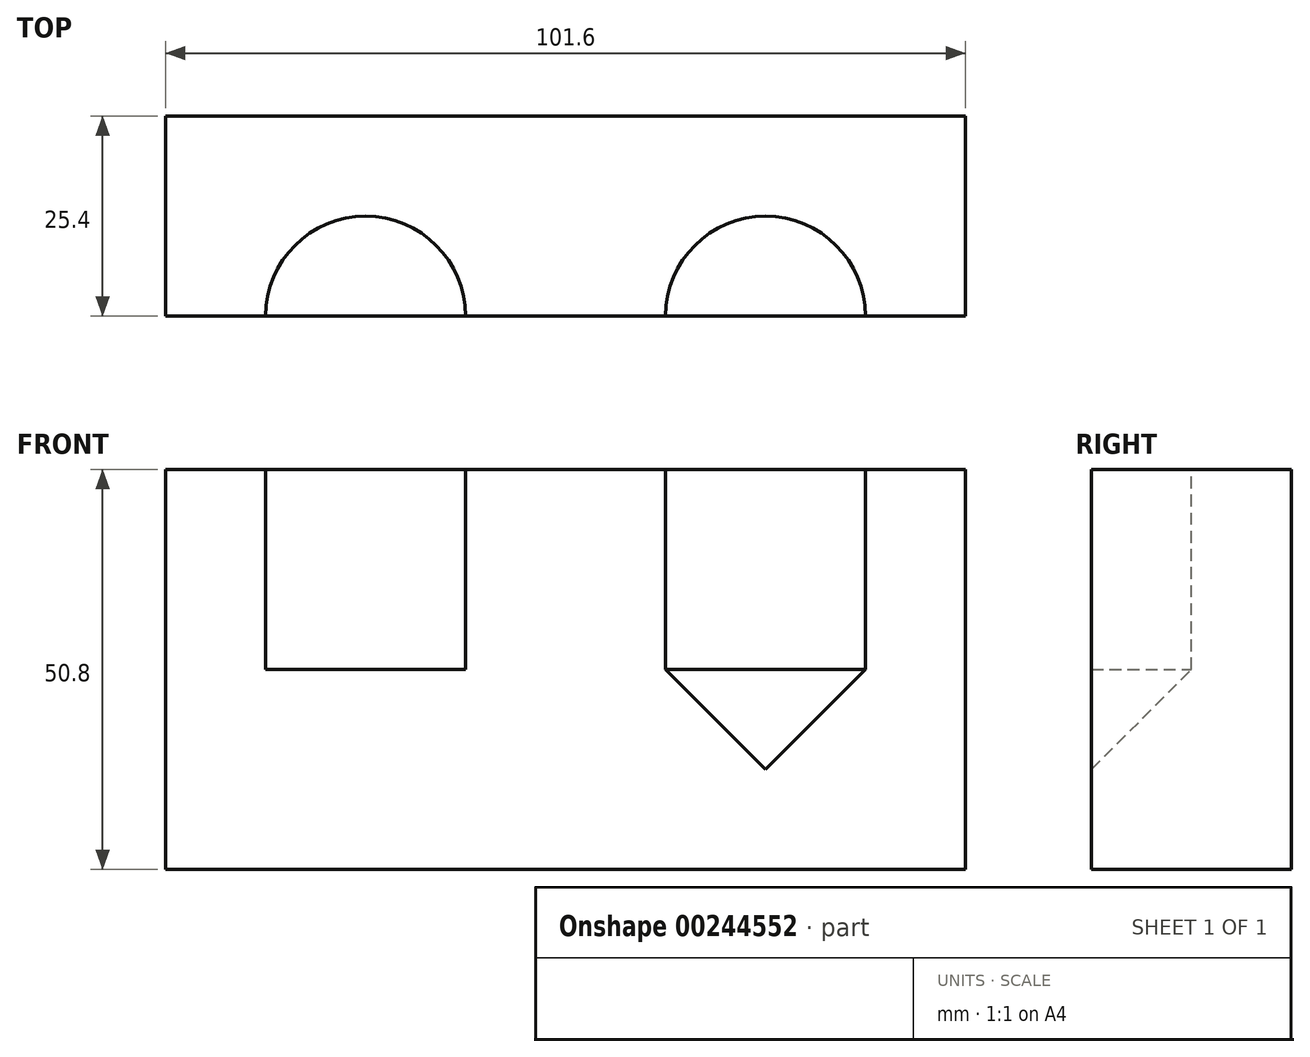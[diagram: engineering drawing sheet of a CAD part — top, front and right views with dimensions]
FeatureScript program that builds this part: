
annotation { "Feature Type Name" : "Feature", "Feature Type Description" : "" }
export const myFeature = defineFeature(function(context is Context, id is Id, definition is map)
    precondition{}
    {
        {
            var Q0;
            Q0=qCreatedBy(makeId("Top.planeOp"),FACE);
            var sketch = newSketch(context, id + "F0", { "sketchPlane" : qUnion([Q0])});
            skLineSegment(sketch, "E0.bottom", {"start": v(50.8, -25.4) * mm, "end": v(-50.8, -25.4) * mm});
            skLineSegment(sketch, "E0.top", {"start": v(50.8, 25.4) * mm, "end": v(-50.8, 25.4) * mm});
            skLineSegment(sketch, "E0.left", {"start": v(50.8, -25.4) * mm, "end": v(50.8, 25.4) * mm});
            skLineSegment(sketch, "E0.right", {"start": v(-50.8, -25.4) * mm, "end": v(-50.8, 25.4) * mm});
            skPoint(sketch, "E0.middle", {"position": v(0, 0) * mm});
            skSolve(sketch);
        }
        {
            var Q0;
            Q0 = qSketchRegion(id + "F0", true);
            extrude(context, id + "F1", {"entities" : qUnion([Q0]), "depth" : 50.8 * mm});
        }
        {
            var Q0;
            Q0=makeQuery(id+"F1.opExtrude","CAP_FACE",FACE,{"disambiguationData":[OSD([sQuery(id+"F0.wireOp",EDGE,"E0.bottom"),sQuery(id+"F0.wireOp",EDGE,"E0.top"),sQuery(id+"F0.wireOp",EDGE,"E0.left"),sQuery(id+"F0.wireOp",EDGE,"E0.right")])],"isStart":false});
            var sketch = newSketch(context, id + "F2", { "sketchPlane" : qUnion([Q0])});
            skCircle(sketch, "E1", {"center": v(-25.4, 0) * mm, "radius": 12.7 * mm});
            skCircle(sketch, "E2", {"center": v(25.4, 0) * mm, "radius": 12.7 * mm});
            skLineSegment(sketch, "E3", {"start": v(-25.4, 0) * mm, "end": v(25.4, 0) * mm, "construction": true});
            skLineSegment(sketch, "E4", {"start": v(0, 0) * mm, "end": v(0, 22.08) * mm, "construction": true});
            skPoint(sketch, "E5", {"position": v(50.8, 0) * mm});
            skSolve(sketch);
        }
        {
            var Q0;
            Q0 = qSketchRegion(id + "F2", true);
            extrude(context, id + "F3", {"entities" : qUnion([Q0]), "operationType" : NewBodyOperationType.REMOVE, "oppositeDirection" : true, "depth" : 25.4 * mm});
        }
        {
            var Q0;
            Q0=makeQuery(id+"F1.opExtrude","CAP_FACE",FACE,{"disambiguationData":[OSD([sQuery(id+"F0.wireOp",EDGE,"E0.bottom"),sQuery(id+"F0.wireOp",EDGE,"E0.top"),sQuery(id+"F0.wireOp",EDGE,"E0.left"),sQuery(id+"F0.wireOp",EDGE,"E0.right")])],"isStart":false});
            var sketch = newSketch(context, id + "F4", { "sketchPlane" : qUnion([Q0])});
            skLineSegment(sketch, "E6.bottom", {"start": v(-50.8, 0) * mm, "end": v(50.8, 0) * mm});
            skLineSegment(sketch, "E6.top", {"start": v(-50.8, -25.4) * mm, "end": v(50.8, -25.4) * mm});
            skLineSegment(sketch, "E6.left", {"start": v(-50.8, 0) * mm, "end": v(-50.8, -25.4) * mm});
            skLineSegment(sketch, "E6.right", {"start": v(50.8, 0) * mm, "end": v(50.8, -25.4) * mm});
            skSolve(sketch);
        }
        {
            var Q0;
            Q0=makeQuery(id+"F3.boolean.opBoolean","COPY",FACE,{"derivedFrom":makeQuery(id+"F3.opExtrude","CAP_FACE",FACE,{"disambiguationData":[OSD([sQuery(id+"F2.wireOp",EDGE,"E2")])],"isStart":false})});
            var sketch = newSketch(context, id + "F5", { "sketchPlane" : qUnion([Q0])});
            skCircle(sketch, "E7.0", {"center": v(25.4, 0) * mm, "radius": 12.7 * mm});
            skSolve(sketch);
        }
        {
            var Q0;
            Q0 = qSketchRegion(id + "F5", true);
            extrude(context, id + "F6", {"entities" : qUnion([Q0]), "operationType" : NewBodyOperationType.REMOVE, "oppositeDirection" : true, "depth" : 13.46 * mm, "hasDraft" : true, "draftAngle" : 45 * degree, "draftPullDirection" : true});
        }
        {
            var Q0;
            Q0 = qSketchRegion(id + "F4", true);
            extrude(context, id + "F7", {"entities" : qUnion([Q0]), "operationType" : NewBodyOperationType.REMOVE, "endBound" : BoundingType.UP_TO_NEXT, "oppositeDirection" : true, "depth" : 25.4 * mm});
        }
    });
